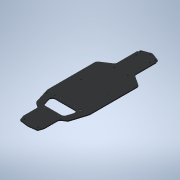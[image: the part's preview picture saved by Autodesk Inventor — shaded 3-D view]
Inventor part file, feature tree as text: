
AUTODESK INVENTOR PART (.ipt)
format: ipt  version: 2020 (Build 240168000, 168)  size: 289,280 bytes
history: native  units: mm (DEFAULTED — no unit token found)
features: hole x3, fillet x3, other x2, extrude x2, sketch x1, mirror x1
ambient origin geometry x8: Origin, YZ Plane, XZ Plane, XY Plane, X Axis, Y Axis, Z Axis, Center Point
bodies: Solid1 (feature_tree)
feature tree (12):
  sketch  "Sketch1"  dims[d1=26.0mm d2=60.0mm d3=58.0mm d4=28.75mm d6=24.0mm d9=44.0mm d13=3.0mm d14=0.0mm d15=15.0mm d16=6.0mm d19=47.5mm d20=256.5mm d21=75.0mm d22=55.0mm d23=31.5mm d24=81.0mm d25=215.0mm d26=260.0mm d27=270.0mm d28=310.0mm d29=324.0mm d30=327.0mm d31=8.0mm d32=2.0mm d43=2.0mm d99=2.0mm d100=0.0mm d101=8.0mm d110=6.0mm d190=9.0mm d191=3.0mm d192=4.0mm d193=7.5mm d195=13.0mm d196=64.0mm d197=23.0mm d198=145.0mm d199=73.0mm d213=-3.0mm d216=3.4mm d217=6.0mm d218=6.3mm d219=2.0mm d220=90.0deg d221=8.0mm d222=20.594885mm d223=3.0mm d224=6.0mm d225=6.0mm d226=2.0mm d227=90.0deg d228=8.0mm d229=20.594885mm d242=1.0mm d243=7.0mm d244=7.0mm d245=39.0mm]
  other  "Bottom"
  hole  "Hole_Centres"  [1 undecoded]
  extrude  "Extrusion1"  Depth=8.0mm
  fillet  "Fillet1"  Radius=28.75mm
  fillet  "Fillet2"  Radius=24.0mm
  other  "5mm Inside"
  extrude  "Extrusion10"  Depth=8.0mm
  fillet  "Fillet9"  Radius=3.0mm
  hole  "Hole2"  [1 undecoded]
  mirror  "Mirror6"
  hole  "Hole3"  [1 undecoded]
note: 3 required parameter values undecoded (feature->parameter linkage not recoverable at this tier; creation-order binding heuristic only, values carry confidence <= 0.55)
